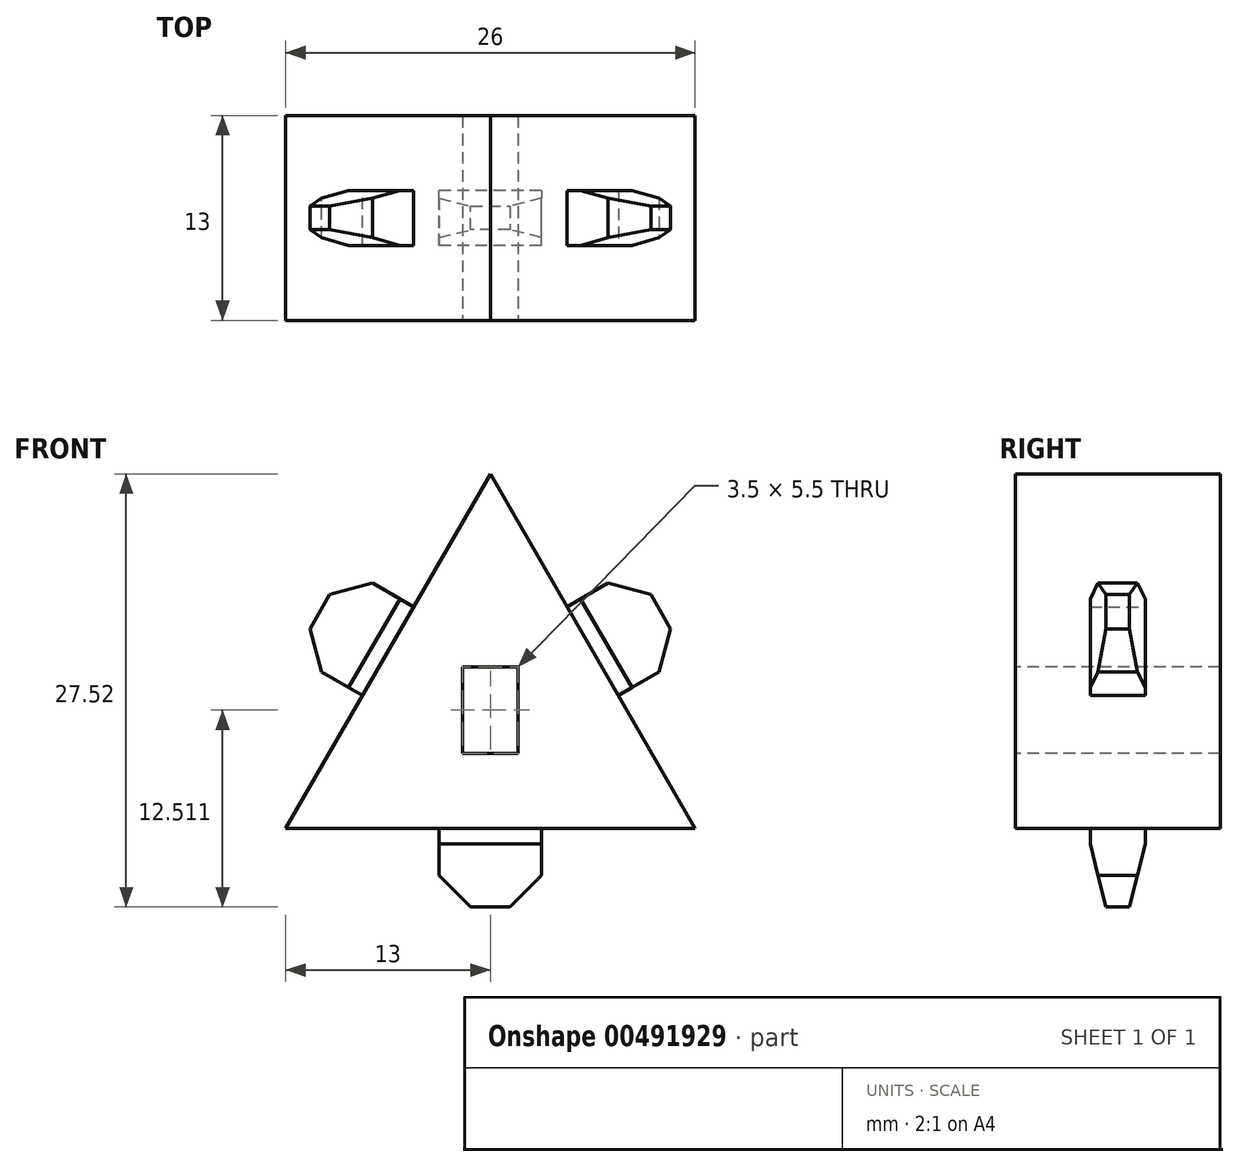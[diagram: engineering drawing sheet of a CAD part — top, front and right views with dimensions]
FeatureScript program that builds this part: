
annotation { "Feature Type Name" : "Feature", "Feature Type Description" : "" }
export const myFeature = defineFeature(function(context is Context, id is Id, definition is map)
    precondition{}
    {
        {
            var Q0;
            Q0=qCreatedBy(makeId("Front.planeOp"),FACE);
            var sketch = newSketch(context, id + "F0", { "sketchPlane" : qUnion([Q0])});
            skLineSegment(sketch, "E0", {"start": v(0, 22.52) * mm, "end": v(-13, 0) * mm});
            skLineSegment(sketch, "E1", {"start": v(-13, 0) * mm, "end": v(13, 0) * mm});
            skLineSegment(sketch, "E2", {"start": v(13, 0) * mm, "end": v(0, 22.52) * mm});
            skPoint(sketch, "E3", {"position": v(0, 7.5) * mm});
            skLineSegment(sketch, "E4", {"start": v(0, 7.5) * mm, "end": v(-13, 0) * mm});
            skLineSegment(sketch, "E5", {"start": v(0, 7.5) * mm, "end": v(13, 0) * mm});
            skLineSegment(sketch, "E6", {"start": v(0, 7.5) * mm, "end": v(0, 22.52) * mm});
            skSolve(sketch);
        }
        {
            var Q0;
            Q0 = qSketchRegion(id + "F0", true);
            extrude(context, id + "F1", {"entities" : qUnion([Q0]), "depth" : 13 * mm, "offsetDistance" : 25 * mm});
        }
        {
            var Q0;
            Q0=makeQuery(id+"F1.opExtrude","CAP_FACE",FACE,{"disambiguationData":[OSD([sQuery(id+"F0.wireOp",EDGE,"E0"),sQuery(id+"F0.wireOp",EDGE,"E1"),sQuery(id+"F0.wireOp",EDGE,"E2")])],"isStart":false});
            var sketch = newSketch(context, id + "F2", { "sketchPlane" : qUnion([Q0])});
            skLineSegment(sketch, "E7.bottom", {"start": v(-1.75, 10.26) * mm, "end": v(1.75, 10.26) * mm});
            skLineSegment(sketch, "E7.top", {"start": v(-1.75, 4.76) * mm, "end": v(1.75, 4.76) * mm});
            skLineSegment(sketch, "E7.left", {"start": v(-1.75, 10.26) * mm, "end": v(-1.75, 4.76) * mm});
            skLineSegment(sketch, "E7.right", {"start": v(1.75, 10.26) * mm, "end": v(1.75, 4.76) * mm});
            skPoint(sketch, "E7.middle", {"position": v(0, 7.51) * mm});
            skSolve(sketch);
        }
        {
            var Q0;
            Q0=makeQuery(id+"F2.imprint","IMPRINT",FACE,{"disambiguationData":[TD([[makeQuery(id+"F2.imprint","IMPRINT",EDGE,{"derivedFrom":sQuery(id+"F2.wireOp",EDGE,"E7.bottom")}),-1.0]])]});
            extrude(context, id + "F3", {"entities" : qUnion([Q0]), "operationType" : NewBodyOperationType.REMOVE, "endBound" : BoundingType.THROUGH_ALL, "oppositeDirection" : true, "depth" : 25 * mm, "offsetDistance" : 25 * mm});
        }
        {
            var Q0;
            Q0=makeQuery(id+"F1.opExtrude","SWEPT_FACE",FACE,{"disambiguationData":[OSD([sQuery(id+"F0.wireOp",EDGE,"E2")])]});
            var sketch = newSketch(context, id + "F4", { "sketchPlane" : qUnion([Q0])});
            skPoint(sketch, "E8", {"position": v(0, 6.5) * mm});
            skLineSegment(sketch, "E9.bottom", {"start": v(-4.75, 3.25) * mm, "end": v(-8.25, 3.25) * mm});
            skLineSegment(sketch, "E9.top", {"start": v(-4.75, 9.75) * mm, "end": v(-8.25, 9.75) * mm});
            skLineSegment(sketch, "E9.left", {"start": v(-4.75, 3.25) * mm, "end": v(-4.75, 9.75) * mm});
            skLineSegment(sketch, "E9.right", {"start": v(-8.25, 3.25) * mm, "end": v(-8.25, 9.75) * mm});
            skPoint(sketch, "E9.middle", {"position": v(-6.5, 6.5) * mm});
            skPoint(sketch, "E9.middle.positionSnap0", {"position": v(-6.5, 19.5) * mm});
            skPoint(sketch, "E9.centerSnap0", {"position": v(-6.5, 19.5) * mm});
            skSolve(sketch);
        }
        {
            var Q0;
            Q0=makeQuery(id+"F1.opExtrude","SWEPT_FACE",FACE,{"disambiguationData":[OSD([sQuery(id+"F0.wireOp",EDGE,"E0")])]});
            var sketch = newSketch(context, id + "F5", { "sketchPlane" : qUnion([Q0])});
            skPoint(sketch, "E10", {"position": v(13, 6.5) * mm});
            skLineSegment(sketch, "E11.bottom", {"start": v(8.25, 3.25) * mm, "end": v(4.75, 3.25) * mm});
            skLineSegment(sketch, "E11.top", {"start": v(8.25, 9.75) * mm, "end": v(4.75, 9.75) * mm});
            skLineSegment(sketch, "E11.left", {"start": v(8.25, 3.25) * mm, "end": v(8.25, 9.75) * mm});
            skLineSegment(sketch, "E11.right", {"start": v(4.75, 3.25) * mm, "end": v(4.75, 9.75) * mm});
            skPoint(sketch, "E11.middle", {"position": v(6.5, 6.5) * mm});
            skPoint(sketch, "E11.middle.positionSnap0", {"position": v(6.5, 19.5) * mm});
            skPoint(sketch, "E11.centerSnap0", {"position": v(6.5, 19.5) * mm});
            skPoint(sketch, "E12", {"position": v(8.25, 6.5) * mm});
            skSolve(sketch);
        }
        {
            var Q0;
            Q0 = qSketchRegion(id + "F4", true);
            extrude(context, id + "F6", {"entities" : qUnion([Q0]), "operationType" : NewBodyOperationType.ADD, "depth" : 5 * mm, "offsetDistance" : 25 * mm});
        }
        {
            var Q0;
            Q0=makeQuery(id+"F5.imprint","IMPRINT",FACE,{"disambiguationData":[TD([[makeQuery(id+"F5.imprint","IMPRINT",EDGE,{"derivedFrom":sQuery(id+"F5.wireOp",EDGE,"E11.bottom")}),-1.0]])]});
            extrude(context, id + "F7", {"entities" : qUnion([Q0]), "operationType" : NewBodyOperationType.ADD, "depth" : 5 * mm, "offsetDistance" : 25 * mm});
        }
        {
            var Q0;
            Q0=makeQuery(id+"F1.opExtrude","SWEPT_FACE",FACE,{"disambiguationData":[OSD([sQuery(id+"F0.wireOp",EDGE,"E1")])]});
            var sketch = newSketch(context, id + "F8", { "sketchPlane" : qUnion([Q0])});
            skPoint(sketch, "E13", {"position": v(-13, 6.5) * mm});
            skLineSegment(sketch, "E14.bottom", {"start": v(3.25, 8.25) * mm, "end": v(-3.25, 8.25) * mm});
            skLineSegment(sketch, "E14.top", {"start": v(3.25, 4.75) * mm, "end": v(-3.25, 4.75) * mm});
            skLineSegment(sketch, "E14.left", {"start": v(3.25, 8.25) * mm, "end": v(3.25, 4.75) * mm});
            skLineSegment(sketch, "E14.right", {"start": v(-3.25, 8.25) * mm, "end": v(-3.25, 4.75) * mm});
            skPoint(sketch, "E14.middle", {"position": v(0, 6.5) * mm});
            skSolve(sketch);
        }
        {
            var Q0;
            Q0=makeQuery(id+"F8.imprint","IMPRINT",FACE,{"disambiguationData":[TD([[makeQuery(id+"F8.imprint","IMPRINT",EDGE,{"derivedFrom":sQuery(id+"F8.wireOp",EDGE,"E14.bottom")}),1.0]])]});
            extrude(context, id + "F9", {"entities" : qUnion([Q0]), "operationType" : NewBodyOperationType.ADD, "depth" : 5 * mm, "offsetDistance" : 25 * mm});
        }
        {
            var Q0;
            Q0=makeQuery(id+"F6.opExtrude","CAP_EDGE",EDGE,{"disambiguationData":[OSD([sQuery(id+"F4.wireOp",EDGE,"E9.right")])],"isStart":false});
            var Q1;
            Q1=makeQuery(id+"F6.opExtrude","CAP_EDGE",EDGE,{"disambiguationData":[OSD([sQuery(id+"F4.wireOp",EDGE,"E9.left")])],"isStart":false});
            var Q2;
            Q2=makeQuery(id+"F9.opExtrude","CAP_EDGE",EDGE,{"disambiguationData":[OSD([sQuery(id+"F8.wireOp",EDGE,"E14.top")])],"isStart":false});
            var Q3;
            Q3=makeQuery(id+"F7.opExtrude","CAP_EDGE",EDGE,{"disambiguationData":[OSD([sQuery(id+"F5.wireOp",EDGE,"E11.right")])],"isStart":false});
            chamfer(context, id + "F10", {"entities" : qUnion([Q0, Q1, Q2, Q3]), "chamferType" : ChamferType.TWO_OFFSETS, "width1" : 4 * mm, "oppositeDirection" : false, "width2" : 1 * mm, "tangentPropagation" : true});
        }
        {
            var Q0;
            Q0=makeQuery(id+"F7.opExtrude","CAP_EDGE",EDGE,{"disambiguationData":[OSD([sQuery(id+"F5.wireOp",EDGE,"E11.left")])],"isStart":false});
            var Q1;
            Q1=makeQuery(id+"F9.opExtrude","CAP_EDGE",EDGE,{"disambiguationData":[OSD([sQuery(id+"F8.wireOp",EDGE,"E14.bottom")])],"isStart":false});
            chamfer(context, id + "F11", {"entities" : qUnion([Q0, Q1]), "chamferType" : ChamferType.TWO_OFFSETS, "width1" : 1 * mm, "oppositeDirection" : false, "width2" : 4 * mm, "tangentPropagation" : true});
        }
        {
            var Q0;
            Q0=makeQuery(id+"F7.opExtrude","CAP_EDGE",EDGE,{"disambiguationData":[OSD([sQuery(id+"F5.wireOp",EDGE,"E11.top")])],"isStart":false});
            var Q1;
            Q1=makeQuery(id+"F7.opExtrude","CAP_EDGE",EDGE,{"disambiguationData":[OSD([sQuery(id+"F5.wireOp",EDGE,"E11.bottom")])],"isStart":false});
            var Q2;
            Q2=makeQuery(id+"F6.opExtrude","CAP_EDGE",EDGE,{"disambiguationData":[OSD([sQuery(id+"F4.wireOp",EDGE,"E9.top")])],"isStart":false});
            var Q3;
            Q3=makeQuery(id+"F6.opExtrude","CAP_EDGE",EDGE,{"disambiguationData":[OSD([sQuery(id+"F4.wireOp",EDGE,"E9.bottom")])],"isStart":false});
            var Q4;
            Q4=makeQuery(id+"F9.opExtrude","CAP_EDGE",EDGE,{"disambiguationData":[OSD([sQuery(id+"F8.wireOp",EDGE,"E14.right")])],"isStart":false});
            var Q5;
            Q5=makeQuery(id+"F9.opExtrude","CAP_EDGE",EDGE,{"disambiguationData":[OSD([sQuery(id+"F8.wireOp",EDGE,"E14.left")])],"isStart":false});
            chamfer(context, id + "F12", {"entities" : qUnion([Q0, Q1, Q2, Q3, Q4, Q5]), "width" : 2 * mm, "tangentPropagation" : true});
        }
    });
